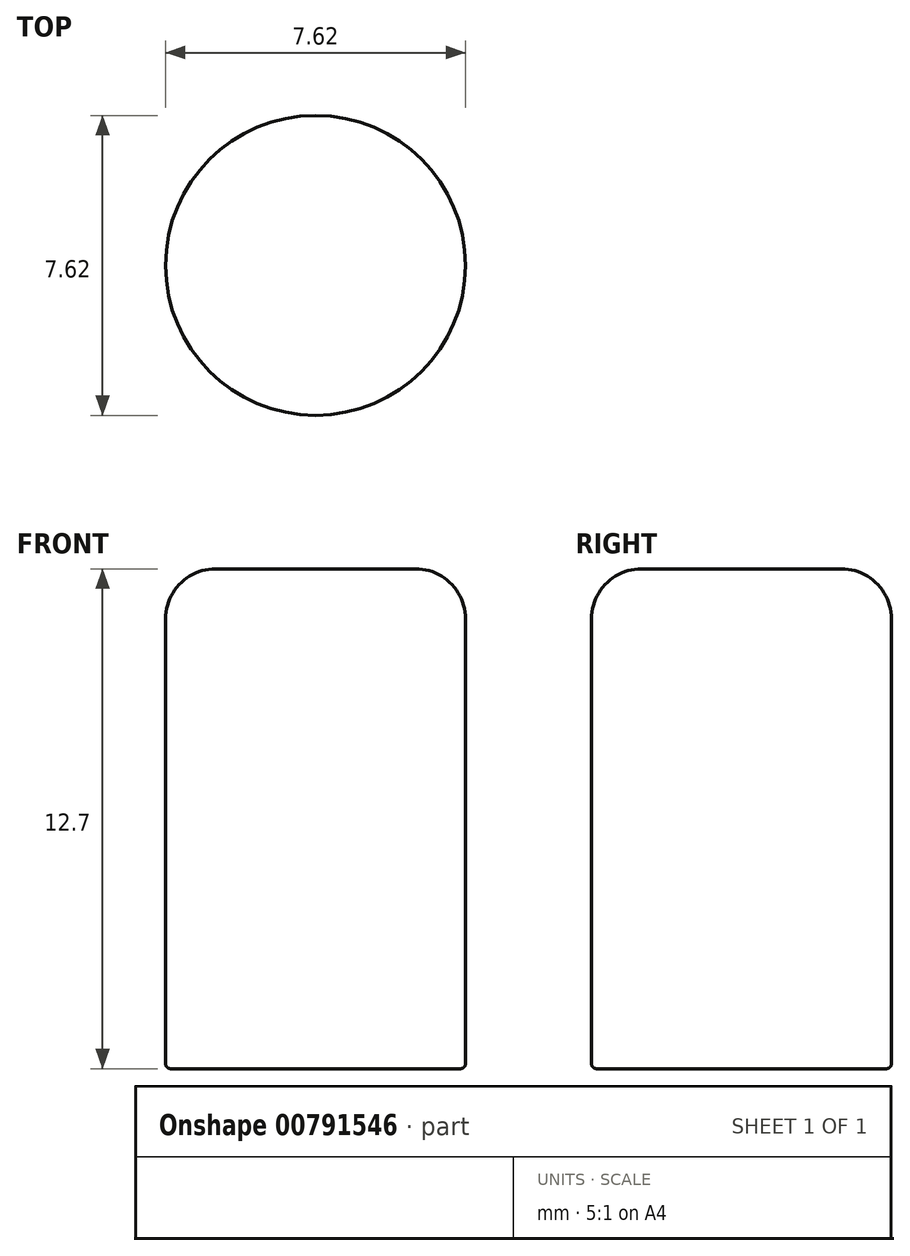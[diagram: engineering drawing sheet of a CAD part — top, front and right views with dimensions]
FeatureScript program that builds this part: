
annotation { "Feature Type Name" : "Feature", "Feature Type Description" : "" }
export const myFeature = defineFeature(function(context is Context, id is Id, definition is map)
    precondition{}
    {
        {
            var Q0;
            Q0=qCreatedBy(makeId("Front.planeOp"),FACE);
            var sketch = newSketch(context, id + "F0", { "sketchPlane" : qUnion([Q0])});
            skLineSegment(sketch, "E0.bottom", {"start": v(0, 0) * mm, "end": v(3.68, 0) * mm});
            skLineSegment(sketch, "E0.top", {"start": v(0.63, 12.7) * mm, "end": v(2.54, 12.7) * mm});
            skLineSegment(sketch, "E0.left", {"start": v(0, 0) * mm, "end": v(0, 12.07) * mm});
            skLineSegment(sketch, "E0.right", {"start": v(3.81, 0.13) * mm, "end": v(3.8, 11.43) * mm});
            skPoint(sketch, "E1.visualSharp", {"position": v(3.8, 12.7) * mm});
            skArc(sketch, "E1.filletArc", {"start": v(3.8, 11.43) * mm, "mid": v(3.44, 12.33) * mm, "end": v(2.54, 12.7) * mm});
            skPoint(sketch, "E2.visualSharp", {"position": v(3.81, 0) * mm});
            skArc(sketch, "E2.filletArc", {"start": v(3.68, 0) * mm, "mid": v(3.77, 0.04) * mm, "end": v(3.81, 0.13) * mm});
            skPoint(sketch, "E3.visualSharp", {"position": v(0, 12.7) * mm});
            skArc(sketch, "E3.filletArc", {"start": v(0.63, 12.7) * mm, "mid": v(0.19, 12.51) * mm, "end": v(0, 12.07) * mm});
            skSolve(sketch);
        }
        {
            var Q0;
            Q0=makeQuery(id+"F0.imprint","IMPRINT",FACE,{"disambiguationData":[TD([[makeQuery(id+"F0.imprint","IMPRINT",EDGE,{"derivedFrom":sQuery(id+"F0.wireOp",EDGE,"E0.bottom")}),1.0]])]});
            var Q1;
            Q1=sQuery(id+"F0.wireOp",EDGE,"E0.left");
            revolve(context, id + "F1", {"surfaceOperationType" : NewSurfaceOperationType.NEW, "entities" : qUnion([Q0]), "axis" : qUnion([Q1]), "revolveType" : RevolveType.FULL});
        }
    });
